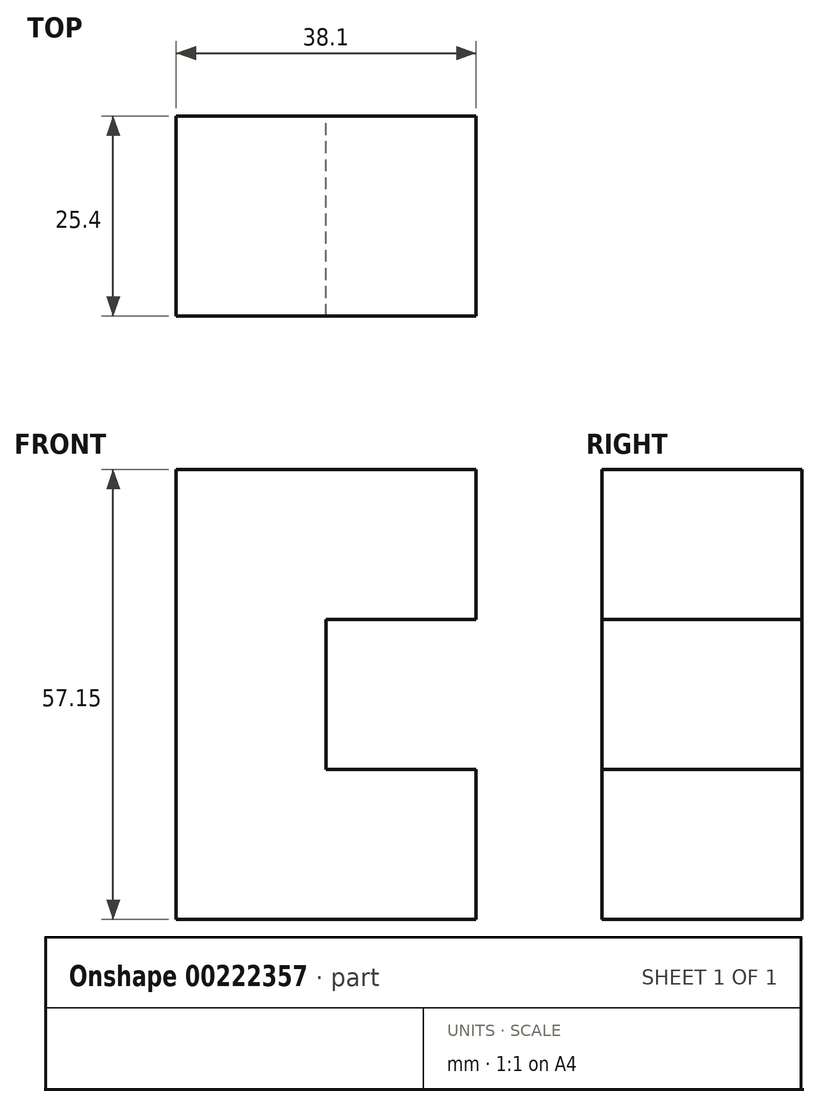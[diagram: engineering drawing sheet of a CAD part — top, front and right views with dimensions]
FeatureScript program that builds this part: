
annotation { "Feature Type Name" : "Feature", "Feature Type Description" : "" }
export const myFeature = defineFeature(function(context is Context, id is Id, definition is map)
    precondition{}
    {
        {
            var Q0;
            Q0=qCreatedBy(makeId("Front.planeOp"),FACE);
            var sketch = newSketch(context, id + "F0", { "sketchPlane" : qUnion([Q0])});
            skLineSegment(sketch, "E0.bottom", {"start": v(-43.35, 10.96) * mm, "end": v(-62.4, 10.96) * mm});
            skLineSegment(sketch, "E0.top", {"start": v(-43.35, 68.11) * mm, "end": v(-62.4, 68.11) * mm});
            skLineSegment(sketch, "E0.left", {"start": v(-43.35, 10.96) * mm, "end": v(-43.35, 68.11) * mm});
            skLineSegment(sketch, "E0.right", {"start": v(-62.4, 10.96) * mm, "end": v(-62.4, 68.11) * mm});
            skPoint(sketch, "E0.middle", {"position": v(-52.87, 39.54) * mm});
            skLineSegment(sketch, "E1.bottom", {"start": v(-24.3, 49.06) * mm, "end": v(-43.35, 49.06) * mm});
            skLineSegment(sketch, "E1.top", {"start": v(-24.3, 68.11) * mm, "end": v(-43.35, 68.11) * mm});
            skLineSegment(sketch, "E1.left", {"start": v(-24.3, 49.06) * mm, "end": v(-24.3, 68.11) * mm});
            skLineSegment(sketch, "E1.right", {"start": v(-43.35, 49.06) * mm, "end": v(-43.35, 68.11) * mm});
            skPoint(sketch, "E1.middle", {"position": v(-33.82, 58.59) * mm});
            skLineSegment(sketch, "E2.bottom", {"start": v(-24.3, 10.96) * mm, "end": v(-43.35, 10.96) * mm});
            skLineSegment(sketch, "E2.top", {"start": v(-24.3, 30.01) * mm, "end": v(-43.35, 30.01) * mm});
            skLineSegment(sketch, "E2.left", {"start": v(-24.3, 10.96) * mm, "end": v(-24.3, 30.01) * mm});
            skLineSegment(sketch, "E2.right", {"start": v(-43.35, 10.96) * mm, "end": v(-43.35, 30.01) * mm});
            skPoint(sketch, "E2.middle", {"position": v(-33.82, 20.49) * mm});
            skSolve(sketch);
        }
        {
            var Q0;
            Q0=qSketchRegion(id+"F0",true);
            extrude(context, id + "F1", {"entities" : qUnion([Q0]), "endBound" : BoundingType.SYMMETRIC, "depth" : 25.4 * mm});
        }
        {
            var Q0;
            Q0=qSketchRegion(id+"F0",true);
            extrude(context, id + "F2", {"entities" : qUnion([Q0]), "operationType" : NewBodyOperationType.ADD, "endBound" : BoundingType.SYMMETRIC, "depth" : 25.4 * mm});
        }
    });
